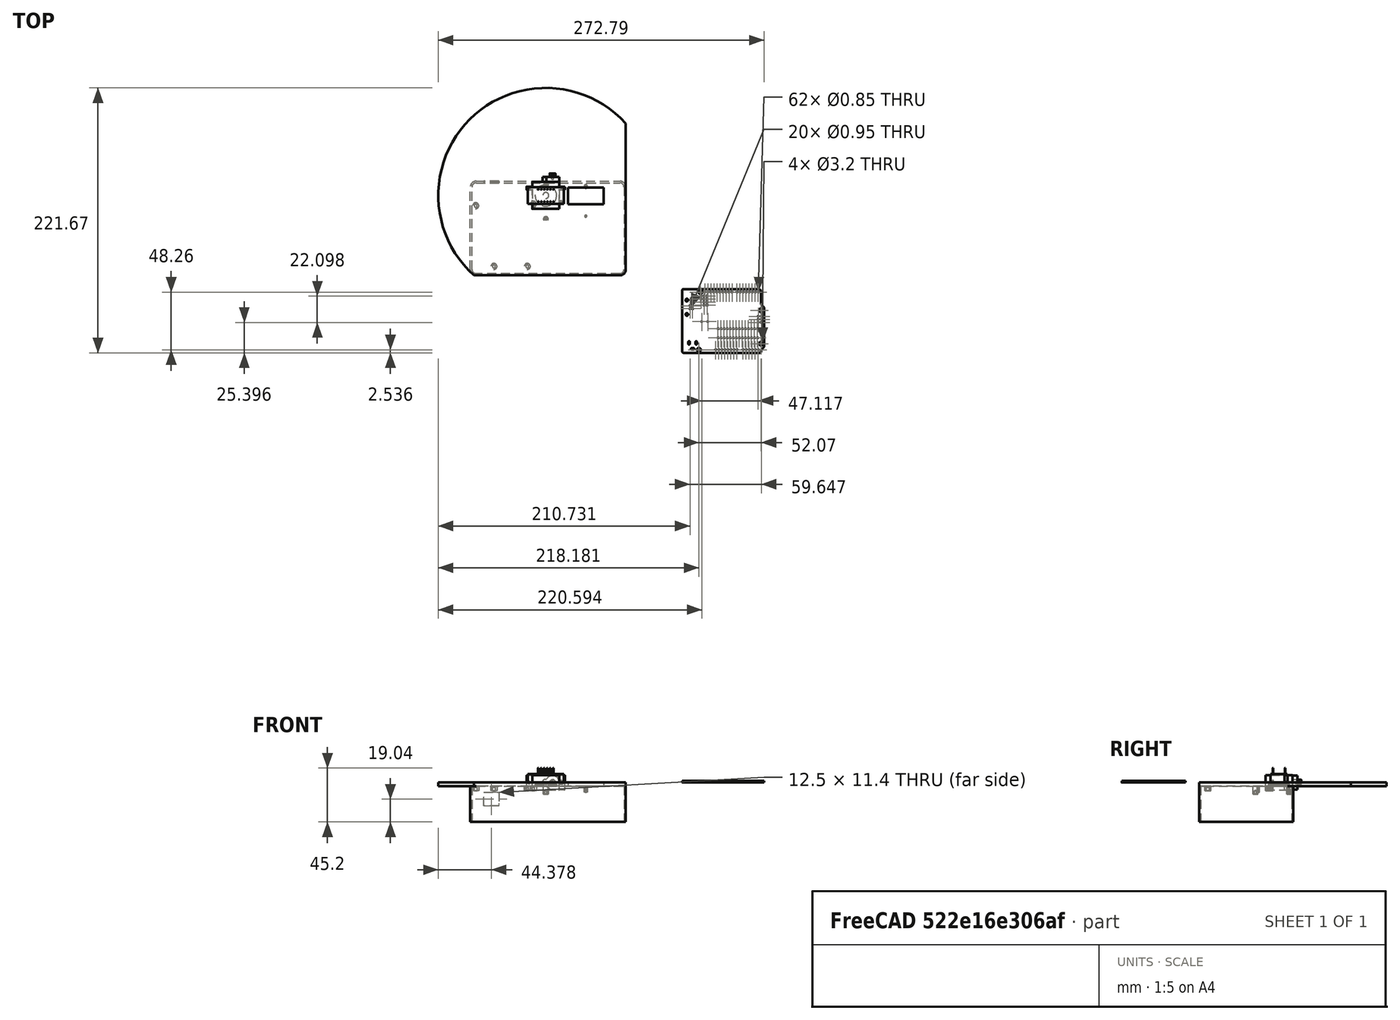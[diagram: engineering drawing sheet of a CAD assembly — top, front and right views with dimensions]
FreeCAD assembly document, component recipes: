
FREECAD ASSEMBLY — COMPONENT RECIPES ("shell.FCStd.bak")

This assembly document has 4 components, labeled P0..P3 below (a component is one placed body or linked part). 1 of them carries a construction recipe — the FreeCAD feature program that regenerates the part from scratch, quoted from this document or its linked companion documents; the rest are supplied as boundary geometry only. No exploded tour is included for this assembly.
COMPONENT P0 — geometry summary ("Corps001"; no construction recipe available for this part):
  bounding box: 30.0 x 14.0 x 12.2 mm
  tessellated surface: 924 triangles
  volume: 3034 mm^3 (59% of its bounding box)
  symmetry: 2-fold rotationally symmetric about the z axis; mirror-symmetric across its x mid-plane, y mid-plane
COMPONENT P1 — geometry summary ("SG90-SERVO001"; no construction recipe available for this part):
  bounding box: 32.2 x 29.8 x 12.5 mm
  tessellated surface: 14,476 triangles
  volume: 7213 mm^3 (60% of its bounding box)
  symmetry: mirror-symmetric across its x mid-plane
COMPONENT P2 — geometry summary ("UNO-TH_Rev3e_PCB001"; no construction recipe available for this part):
  bounding box: 68.6 x 53.4 x 1.5 mm
  tessellated surface: 16,748 triangles
  volume: 5303 mm^3 (96% of its bounding box)
  symmetry: mirror-symmetric across its z mid-plane
COMPONENT P3 — recipe-attached ("shell001", modeled in this document).
Construction recipe (the document's own serialized feature program — sketch geometry with constraints, then the solid features built on it; lengths are millimeters unless a unit is written):

FEATURE [Sketcher::SketchObject] Sketch
  ArcFitTolerance = 1e-06
  AttachmentSupport = -> [XY_Plane]
  FullyConstrained = true
  MakeInternals = false
  MapMode = 5
  sketch-geometry (14):
    g0: LineSegment StartX=18.4415 StartY=6.5 StartZ=0 EndX=18.4415 EndY=-7.5 EndZ=0
    g1: LineSegment StartX=18.4415 StartY=-7.5 StartZ=0 EndX=48.4415 EndY=-7.5 EndZ=0
    g2: LineSegment StartX=48.4415 StartY=-7.5 StartZ=0 EndX=48.4415 EndY=6.5 EndZ=0
    g3: LineSegment StartX=48.4415 StartY=6.5 StartZ=0 EndX=18.4415 EndY=6.5 EndZ=0
    g4: GeomPoint [constr] X=33.4415 Y=-0.5 Z=0
    g5: ArcOfCircle CenterX=0 CenterY=0 CenterZ=0 NormalX=0 NormalY=0 NormalZ=1 AngleXU=0 Radius=90 StartAngle=0.733038 EndAngle=3.97935
    g6: Circle CenterX=0 CenterY=0 CenterZ=0 NormalX=0 NormalY=0 NormalZ=1 AngleXU=0 Radius=2.5
    g7: LineSegment [constr] StartX=0 StartY=0 StartZ=0 EndX=66.883 EndY=60.2218 EndZ=0
    g8: LineSegment [constr] StartX=0 StartY=0 StartZ=0 EndX=-60.2218 EndY=-66.883 EndZ=0
    g9: LineSegment StartX=66.883 StartY=60.2218 StartZ=0 EndX=66.883 EndY=-61.883 EndZ=0
    g10: LineSegment StartX=61.883 StartY=-66.883 StartZ=0 EndX=-60.2218 EndY=-66.883 EndZ=0
    g11: ArcOfCircle CenterX=61.883 CenterY=-61.883 CenterZ=0 NormalX=0 NormalY=0 NormalZ=1 AngleXU=0 Radius=5 StartAngle=4.71239 EndAngle=6.28319
    g12: LineSegment [constr] StartX=48.4415 StartY=3.78 StartZ=0 EndX=66.883 EndY=3.78 EndZ=0
    g13: LineSegment [constr] StartX=0 StartY=0 StartZ=0 EndX=18.4415 EndY=0 EndZ=0
  constraints (37):
    c: Coincident(g0,g1)
    c: Coincident(g1,g2)
    c: Coincident(g2,g3)
    c: Coincident(g3,g0)
    c: Vertical(g2)
    c: Horizontal(g1)
    c: Horizontal(g3)
    c: Symmetric(g2,g0,g4)
    c: DistanceX(g1,g1) = 30
    c: DistanceY(g2,g2) = 14
    c: Radius(g5) = 90
    c: Coincident(g5,g-1)
    c: Coincident(g6,g5)
    c: Diameter(g6) = 5
    c: Coincident(g7,g5)
    c: Coincident(g8,g5)
    c: Angle(g8,g-1,g5) = 2.30383
    c: Vertical(g9)
    c: Horizontal(g10)
    c: Angle(g-1,g7) = 0.733038
    c: Tangent(g9,g11) = 1.5708
    c: Tangent(g10,g11) = 1.5708
    c: Radius(g11) = 5
    c: Coincident(g5,g8)
    c: Coincident(g5,g7)
    c: Coincident(g9,g5)
    c: Coincident(g10,g5)
    c: PointOnObject(g12,g9)
    c: PointOnObject(g12,g2)
    c: DistanceY(g-1,g12) = 3.78
    c: Horizontal(g12,g12)
    c: Coincident(g13,g5)
    c: Vertical(g13,g0)
    c: PointOnObject(g13,g-1)
    c: Equal(g12,g13)
    c: Perpendicular(g0,g1)
    c: DistanceY(g-1,g4) = -0.5
FEATURE [PartDesign::Pad] Pad
  Direction = (0,0,1)
  Length = 3
  Length2 = 10
  Profile = -> Sketch
  ReferenceAxis = -> Sketch [N_Axis]
  Refine = true
  Reversed = true
  Suppressed = false
  Type = 0
FEATURE [Sketcher::SketchObject] Sketch001
  ArcFitTolerance = 1e-06
  FullyConstrained = true
  MakeInternals = false
  MapMode = 5
  Placement = pos=(0,0,-3) rot=(1,0,0;3.14159rad)
  sketch-geometry (1):
    g0: Circle CenterX=0 CenterY=0 CenterZ=0 NormalX=0 NormalY=0 NormalZ=1 AngleXU=0 Radius=9
  constraints (2):
    c: Diameter(g0) = 18
    c: Coincident(g0,g-1)
FEATURE [Sketcher::SketchObject] Sketch003
  ArcFitTolerance = 1e-06
  FullyConstrained = true
  MakeInternals = false
  MapMode = 5
  Placement = pos=(0,0,-3) rot=(1,0,0;3.14159rad)
  sketch-geometry (3):
    g0: Circle CenterX=1e-16 CenterY=19.72 CenterZ=0 NormalX=0 NormalY=0 NormalZ=1 AngleXU=0 Radius=2
    g1: Circle CenterX=0 CenterY=-8.53 CenterZ=0 NormalX=0 NormalY=0 NormalZ=1 AngleXU=0 Radius=2
    g2: LineSegment [constr] StartX=1e-16 StartY=19.72 StartZ=0 EndX=0 EndY=-8.53 EndZ=0
  constraints (8):
    c: Diameter(g0) = 4
    c: Diameter(g1) = 4
    c: Distance(g0,g1) = 28.25
    c: Distance(g1,g-1) = 8.53
    c: DistanceX(g1,g-1) = 0
    c: Coincident(g2,g0)
    c: Coincident(g2,g1)
    c: PointOnObject(g-1,g2)
FEATURE [PartDesign::Pocket] Pocket001
  BaseFeature = -> Pad
  Direction = (0,0,1)
  Length = 1.5
  Length2 = 5
  Profile = -> Sketch001
  ReferenceAxis = -> Sketch001 [N_Axis]
  Refine = true
  Suppressed = false
  Type = 0
FEATURE [Sketcher::SketchObject] Sketch002
  ArcFitTolerance = 1e-06
  AttachmentSupport = -> [Pocket001]
  ExternalGeometry = -> [Pocket001]
  FullyConstrained = true
  MakeInternals = false
  MapMode = 5
  Placement = pos=(0,0,-3) rot=(1,0,0;3.14159rad)
  sketch-geometry (5):
    g0: Circle CenterX=-43.4418 CenterY=59.423 CenterZ=0 NormalX=0 NormalY=0 NormalZ=1 AngleXU=0 Radius=2.5
    g1: Circle CenterX=-15.5018 CenterY=59.423 CenterZ=0 NormalX=0 NormalY=0 NormalZ=1 AngleXU=0 Radius=2.5
    g2: Circle CenterX=-10.4218 CenterY=7.35303 CenterZ=0 NormalX=0 NormalY=0 NormalZ=1 AngleXU=0 Radius=2.5
    g3: Circle CenterX=-58.6818 CenterY=8.62303 CenterZ=0 NormalX=0 NormalY=0 NormalZ=1 AngleXU=0 Radius=2.5
    g4: GeomPoint X=-61.2218 Y=-6.61697 Z=0
  constraints (14):
    c: Equal(g1,g0)
    c: Equal(g0,g3)
    c: Equal(g3,g2)
    c: Diameter(g3) = 5
    c: DistanceY(g4,g3) = 15.24
    c: DistanceY(g4,g0) = 66.04
    c: Horizontal(g0,g1)
    c: DistanceX(g4,g3) = 2.54
    c: DistanceX(g4,g2) = 50.8
    c: DistanceX(g4,g0) = 17.78
    c: DistanceX(g4,g1) = 45.72
    c: DistanceX(g4,g-3) = 1
    c: DistanceY(g4,g-3) = 73.5
    c: DistanceY(g4,g2) = 13.97
FEATURE [PartDesign::Pad] Pad005
  BaseFeature = -> Pocket001
  Direction = (0,0,-1)
  Length = 4
  Length2 = 10
  Profile = -> Sketch002
  ReferenceAxis = -> Sketch002 [N_Axis]
  Refine = true
  Suppressed = false
  Type = 0
FEATURE [PartDesign::Pad] Pad002
  BaseFeature = -> Pad005
  Direction = (0,-1e-16,-1)
  Length = 6.75
  Length2 = 10
  Profile = -> Sketch003
  ReferenceAxis = -> Sketch003 [N_Axis]
  Refine = true
  Suppressed = false
  Type = 0
FEATURE [Sketcher::SketchObject] Sketch005
  ArcFitTolerance = 1e-06
  ExternalGeometry = -> [Sketch002]
  FullyConstrained = true
  MakeInternals = false
  MapMode = 5
  Placement = pos=(0,12.03,0) rot=(0,0.707107,0.707107;3.14159rad)
  sketch-geometry (4):
    g0: LineSegment StartX=51.8718 StartY=-19.66 StartZ=0 EndX=51.8718 EndY=-8.26 EndZ=0
    g1: LineSegment StartX=51.8718 StartY=-8.26 StartZ=0 EndX=39.3718 EndY=-8.26 EndZ=0
    g2: LineSegment StartX=39.3718 StartY=-8.26 StartZ=0 EndX=39.3718 EndY=-19.66 EndZ=0
    g3: LineSegment StartX=39.3718 StartY=-19.66 StartZ=0 EndX=51.8718 EndY=-19.66 EndZ=0
  constraints (12):
    c: Coincident(g0,g1)
    c: Coincident(g1,g2)
    c: Coincident(g2,g3)
    c: Coincident(g3,g0)
    c: Vertical(g0)
    c: Vertical(g2)
    c: Horizontal(g1)
    c: Horizontal(g3)
    c: DistanceY(g1,g-3) = 5.26
    c: DistanceX(g0,g-3) = 9.35
    c: DistanceX(g1,g1) = 12.5
    c: DistanceY(g2,g2) = 11.4
FEATURE [PartDesign::Hole] Hole001
  BaseFeature = -> Pad002
  CustomThreadClearance = 0
  Depth = 3
  DepthType = 0
  Diameter = 1.6
  DrillForDepth = false
  DrillPoint = 1
  DrillPointAngle = 118
  HoleCutCountersinkAngle = 90
  HoleCutCustomValues = false
  HoleCutDepth = 0
  HoleCutDiameter = 6.1
  HoleCutType = 0
  ModelThread = false
  Profile = -> Pad002 [Face26,Face24]
  Refine = true
  Suppressed = false
  Tapered = false
  TaperedAngle = 90
  ThreadClass = 0
  ThreadDepth = 3
  ThreadDepthType = 0
  ThreadDirection = 0
  ThreadFit = 0
  ThreadSize = 6
  ThreadType = 1
  Threaded = true
  UseCustomThreadClearance = false
FEATURE [PartDesign::Pad] Pad003
  BaseFeature = -> Hole001
  Direction = (0,-1e-16,-1)
  Length = 3
  Length2 = 10
  Profile = -> Sketch003 [Edge2]
  ReferenceAxis = -> Sketch003 [N_Axis]
  Refine = true
  Reversed = true
  Suppressed = false
  Type = 0
FEATURE [Sketcher::SketchObject] Sketch004
  ArcFitTolerance = 1e-06
  AttachmentSupport = -> [Pad003]
  ExternalGeometry = -> [Pad003]
  FullyConstrained = true
  MakeInternals = false
  MapMode = 5
  Placement = pos=(0,0,-3) rot=(1,0,0;3.14159rad)
  sketch-geometry (22):
    g0: LineSegment StartX=-63.2708 StartY=61.883 StartZ=0 EndX=-63.2708 EndY=-7.03 EndZ=0
    g1: LineSegment StartX=-58.2708 StartY=-12.03 StartZ=0 EndX=61.883 EndY=-12.03 EndZ=0
    g2: LineSegment StartX=66.883 StartY=-7.03 StartZ=0 EndX=66.883 EndY=61.883 EndZ=0
    g3: LineSegment StartX=61.883 StartY=66.883 StartZ=0 EndX=-58.2708 EndY=66.883 EndZ=0
    g4: ArcOfCircle CenterX=61.883 CenterY=61.883 CenterZ=0 NormalX=0 NormalY=0 NormalZ=1 AngleXU=0 Radius=5 StartAngle=3.1571e-08 EndAngle=1.5708
    g5: LineSegment StartX=-61.7708 StartY=61.883 StartZ=0 EndX=-61.7708 EndY=-7.03 EndZ=0
    g6: LineSegment StartX=-58.2708 StartY=-10.53 StartZ=0 EndX=61.883 EndY=-10.53 EndZ=0
    g7: LineSegment StartX=65.383 StartY=-7.03 StartZ=0 EndX=65.383 EndY=61.883 EndZ=0
    g8: LineSegment StartX=61.883 StartY=65.383 StartZ=0 EndX=-58.2708 EndY=65.383 EndZ=0
    g9: ArcOfCircle CenterX=61.883 CenterY=61.883 CenterZ=0 NormalX=0 NormalY=0 NormalZ=1 AngleXU=0 Radius=3.5 StartAngle=4e-16 EndAngle=1.5708
    g10: GeomPoint [constr] X=65.383 Y=65.383 Z=0
    g11: ArcOfCircle CenterX=-58.2708 CenterY=-7.03 CenterZ=0 NormalX=0 NormalY=0 NormalZ=1 AngleXU=0 Radius=3.5 StartAngle=3.14159 EndAngle=4.71239
    g12: GeomPoint [constr] X=-61.7708 Y=-10.53 Z=0
    g13: ArcOfCircle CenterX=-58.2708 CenterY=-7.03 CenterZ=0 NormalX=0 NormalY=0 NormalZ=1 AngleXU=0 Radius=5 StartAngle=3.14159 EndAngle=4.71239
    g14: GeomPoint [constr] X=-63.2708 Y=-12.03 Z=0
    g15: ArcOfCircle CenterX=61.883 CenterY=-7.03 CenterZ=0 NormalX=0 NormalY=0 NormalZ=1 AngleXU=0 Radius=3.5 StartAngle=4.71239 EndAngle=6.28319
    g16: GeomPoint [constr] X=65.383 Y=-10.53 Z=0
    g17: ArcOfCircle CenterX=61.883 CenterY=-7.03 CenterZ=0 NormalX=0 NormalY=0 NormalZ=1 AngleXU=0 Radius=5 StartAngle=4.71239 EndAngle=6.28319
    g18: GeomPoint [constr] X=66.883 Y=-12.03 Z=0
    g19: ArcOfCircle CenterX=-58.2708 CenterY=61.883 CenterZ=0 NormalX=0 NormalY=0 NormalZ=1 AngleXU=0 Radius=3.5 StartAngle=1.5708 EndAngle=3.14159
    g20: GeomPoint [constr] X=-61.7708 Y=65.383 Z=0
    g21: ArcOfCircle CenterX=-58.2708 CenterY=61.883 CenterZ=0 NormalX=0 NormalY=0 NormalZ=1 AngleXU=0 Radius=5 StartAngle=1.5708 EndAngle=3.14159
  constraints (52):
    c: PointOnObject(g18,g-4)
    c: Horizontal(g1)
    c: Perpendicular(g0,g1)
    c: Coincident(g4,g3)
    c: Coincident(g-5,g4)
    c: Coincident(g4,g2)
    c: Coincident(g-5,g3)
    c: DistanceX(g2,g-5) = 0
    c: Vertical(g5)
    c: Vertical(g7)
    c: Horizontal(g6)
    c: Horizontal(g8)
    c: Distance(g3,g8) = 1.5
    c: Distance(g14,g6) = 1.5
    c: Tangent(g6,g-6)
    c: Distance(g18,g7) = 1.5
    c: PointOnObject(g10,g8)
    c: PointOnObject(g10,g7)
    c: Tangent(g8,g9) = -1.5708
    c: Tangent(g7,g9) = -1.5708
    c: Distance(g4,g9) = 1.5
    c: PointOnObject(g12,g6)
    c: PointOnObject(g12,g5)
    c: Tangent(g6,g11) = -1.5708
    c: Tangent(g5,g11) = -1.5708
    c: PointOnObject(g14,g1)
    c: PointOnObject(g14,g0)
    c: Tangent(g1,g13) = -1.5708
    c: Tangent(g0,g13) = -1.5708
    c: Vertical(g6,g1)
    c: Distance(g11,g13) = 5
    c: PointOnObject(g16,g6)
    c: PointOnObject(g16,g7)
    c: Tangent(g6,g15) = -1.5708
    c: Tangent(g7,g15) = -1.5708
    c: PointOnObject(g18,g1)
    c: PointOnObject(g18,g2)
    c: Tangent(g1,g17) = -1.5708
    c: Tangent(g2,g17) = -1.5708
    c: Vertical(g1,g6)
    c: Distance(g15,g17) = 5
    c: PointOnObject(g20,g8)
    c: PointOnObject(g20,g5)
    c: Tangent(g8,g19) = -1.5708
    c: Tangent(g5,g19) = -1.5708
    c: Tangent(g3,g21) = -1.5708
    c: Tangent(g0,g21) = -1.5708
    c: Vertical(g8,g3)
    c: Horizontal(g5,g0)
    c: Distance(g21,g19) = 1.5
    c: Distance(g19,g21) = 5
    c: Tangent(g21,g-7)
FEATURE [PartDesign::Pad] Pad006
  BaseFeature = -> Pad003
  Direction = (0,0,-1)
  Length = 30
  Length2 = 10
  Profile = -> Sketch004
  ReferenceAxis = -> Sketch004 [N_Axis]
  Refine = true
  Suppressed = false
  Type = 0
FEATURE [PartDesign::Pocket] Pocket
  BaseFeature = -> Pad006
  Direction = (-1e-16,-1,2e-16)
  Length = 5
  Length2 = 5
  Profile = -> Sketch005
  ReferenceAxis = -> Sketch005 [N_Axis]
  Refine = true
  Suppressed = false
  Type = 0
FEATURE [PartDesign::Hole] Hole
  BaseFeature = -> Pocket
  CustomThreadClearance = 0
  Depth = 3
  DepthType = 0
  Diameter = 2.4
  DrillForDepth = false
  DrillPoint = 1
  DrillPointAngle = 118
  HoleCutCountersinkAngle = 90
  HoleCutCustomValues = false
  HoleCutDepth = 0
  HoleCutDiameter = 6.1
  HoleCutType = 0
  ModelThread = false
  Profile = -> Pocket [Face42,Face40,Face41,Face44]
  Refine = true
  Suppressed = false
  Tapered = false
  TaperedAngle = 90
  ThreadClass = 0
  ThreadDepth = 3
  ThreadDepthType = 0
  ThreadDirection = 0
  ThreadFit = 0
  ThreadSize = 6
  ThreadType = 1
  Threaded = false
  UseCustomThreadClearance = false
FEATURE [Sketcher::SketchObject] Sketch006
  ArcFitTolerance = 1e-06
  AttachmentSupport = -> [Pad006]
  ExternalGeometry = -> [Pad006]
  FullyConstrained = true
  MakeInternals = false
  MapMode = 5
  Placement = pos=(0,0,-3) rot=(1,0,0;3.14159rad)
  sketch-geometry (2):
    g0: Circle CenterX=33.4415 CenterY=-7.7 CenterZ=0 NormalX=0 NormalY=0 NormalZ=1 AngleXU=0 Radius=1.3
    g1: Circle CenterX=33.4415 CenterY=17.3 CenterZ=0 NormalX=0 NormalY=0 NormalZ=1 AngleXU=0 Radius=0.9
  constraints (6):
    c: Diameter(g0) = 2.6
    c: Diameter(g1) = 1.8
    c: DistanceX(g-3,g0) = 15
    c: Vertical(g1,g0)
    c: DistanceY(g0,g1) = 25
    c: Distance(g0,g-3) = 1.2
FEATURE [PartDesign::Pad] Pad007
  BaseFeature = -> Hole
  Direction = (0,0,-1)
  Length = 5
  Length2 = 10
  Profile = -> Sketch006
  ReferenceAxis = -> Sketch006 [N_Axis]
  Refine = true
  Suppressed = false
  Type = 0
FEATURE [PartDesign::Hole] Hole002
  BaseFeature = -> Pad007
  CustomThreadClearance = 0
  Depth = 3
  DepthType = 0
  Diameter = 1.2
  DrillForDepth = false
  DrillPoint = 1
  DrillPointAngle = 118
  HoleCutCountersinkAngle = 90
  HoleCutCustomValues = false
  HoleCutDepth = 0
  HoleCutDiameter = 6.1
  HoleCutType = 0
  ModelThread = false
  Profile = -> Pad007 [Face48,Face50]
  Refine = true
  Suppressed = false
  Tapered = false
  TaperedAngle = 90
  ThreadClass = 0
  ThreadDepth = 3
  ThreadDepthType = 0
  ThreadDirection = 0
  ThreadFit = 0
  ThreadSize = 0
  ThreadType = 1
  Threaded = false
  UseCustomThreadClearance = false
FEATURE [PartDesign::Body] Body  label="shell"
  AllowCompound = false
  Group = -> [Sketch,Pad,Sketch001,Pocket001,Sketch002,Pad005,Sketch003,Pad002,Hole001,Pad003,Sketch004,Pad006,Sketch005,Pocket,Hole,Sketch006,Pad007,Hole002]
  Origin = -> Origin
  Tip = -> Hole002
PROVENANCE & LICENSES
A FreeCAD (.FCStd) document from a public repository crawl; recipes are the document's own serialized feature recipes (and, for linked parts, companion documents' recipes).
License: as declared in the source repository (recorded in the dataset sidecar).
